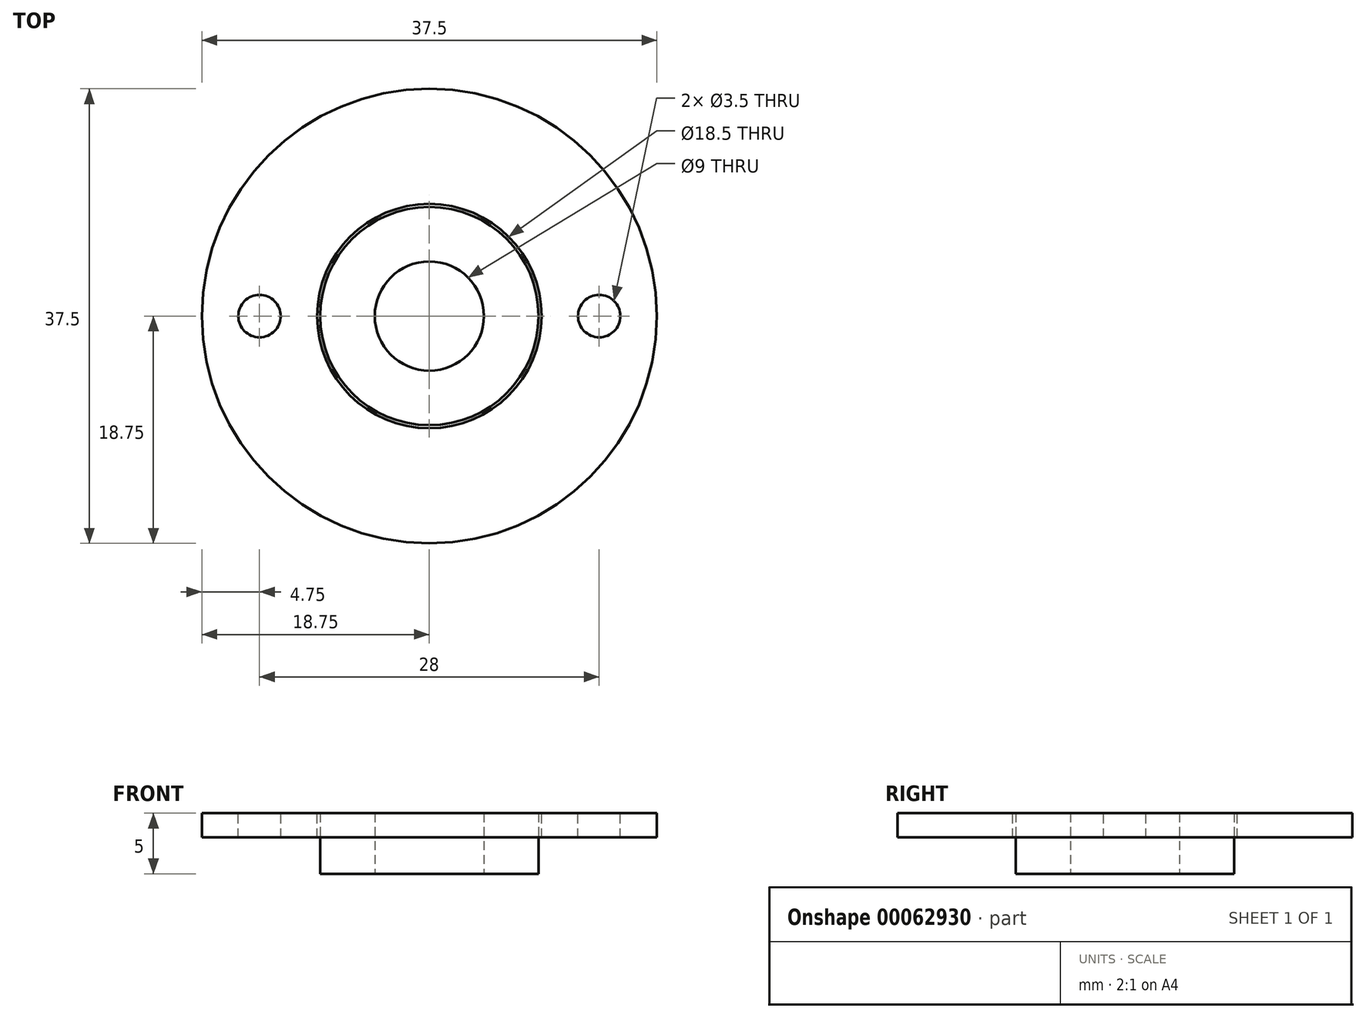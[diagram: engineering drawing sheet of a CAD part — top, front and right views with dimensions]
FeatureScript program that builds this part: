
annotation { "Feature Type Name" : "Feature", "Feature Type Description" : "" }
export const myFeature = defineFeature(function(context is Context, id is Id, definition is map)
    precondition{}
    {
        {
            var Q0;
            Q0=qCreatedBy(makeId("Top.planeOp"),FACE);
            var sketch = newSketch(context, id + "F0", { "sketchPlane" : qUnion([Q0])});
            skCircle(sketch, "E0", {"center": v(0, 0) * mm, "radius": 4.5 * mm});
            skCircle(sketch, "E1", {"center": v(0, 0) * mm, "radius": 9 * mm});
            skSolve(sketch);
        }
        {
            var Q0;
            Q0 = qSketchRegion(id + "F0", true);
            extrude(context, id + "F1", {"entities" : qUnion([Q0]), "depth" : 5 * mm});
        }
        {
            var Q0;
            Q0=makeQuery(id+"F1.opExtrude","CAP_FACE",FACE,{"disambiguationData":[OSD([sQuery(id+"F0.wireOp",EDGE,"E0"),sQuery(id+"F0.wireOp",EDGE,"E1")])],"isStart":false});
            var sketch = newSketch(context, id + "F2", { "sketchPlane" : qUnion([Q0])});
            skCircle(sketch, "E2", {"center": v(0, 0) * mm, "radius": 9.25 * mm});
            skCircle(sketch, "E3", {"center": v(0, 0) * mm, "radius": 18.75 * mm});
            skCircle(sketch, "E4", {"center": v(-14, 0) * mm, "radius": 1.75 * mm});
            skCircle(sketch, "E5", {"center": v(14, 0) * mm, "radius": 1.75 * mm});
            skSolve(sketch);
        }
        {
            var Q0;
            Q0 = qSketchRegion(id + "F2", true);
            extrude(context, id + "F3", {"entities" : qUnion([Q0]), "oppositeDirection" : true, "depth" : 2 * mm});
        }
    });
